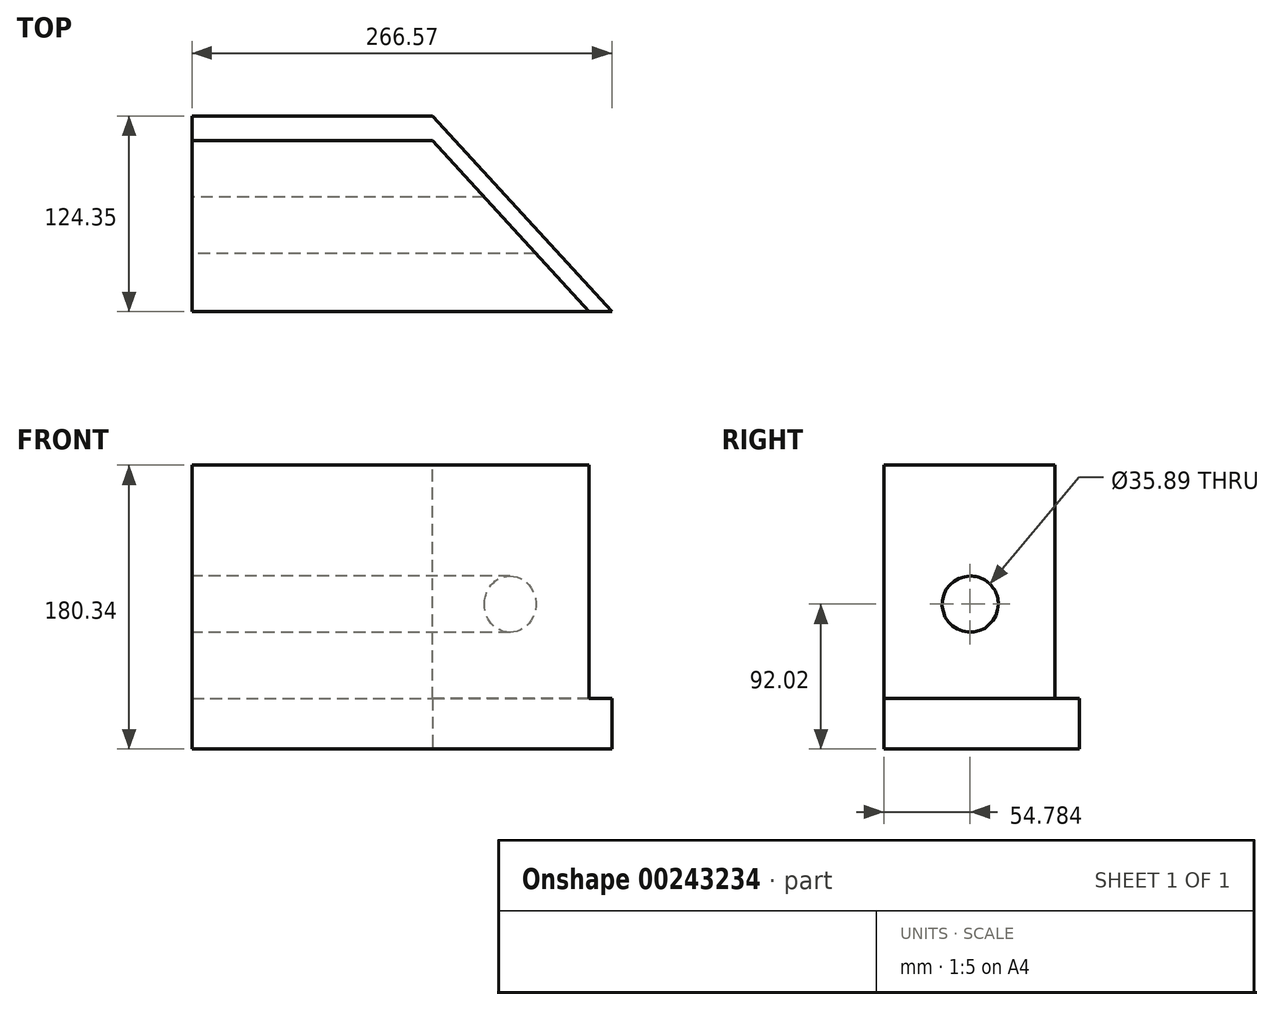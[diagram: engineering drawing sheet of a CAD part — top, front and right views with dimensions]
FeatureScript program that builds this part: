
annotation { "Feature Type Name" : "Feature", "Feature Type Description" : "" }
export const myFeature = defineFeature(function(context is Context, id is Id, definition is map)
    precondition{}
    {
        {
            var Q0;
            Q0=qCreatedBy(makeId("Top.planeOp"),FACE);
            var sketch = newSketch(context, id + "F0", { "sketchPlane" : qUnion([Q0])});
            skLineSegment(sketch, "E0.bottom", {"start": v(-76.3, 35.97) * mm, "end": v(76.5, 35.97) * mm});
            skLineSegment(sketch, "E0.top", {"start": v(-76.3, -72.6) * mm, "end": v(76.5, -72.6) * mm});
            skLineSegment(sketch, "E0.left", {"start": v(-76.3, 35.97) * mm, "end": v(-76.3, -72.6) * mm});
            skLineSegment(sketch, "E1", {"start": v(76.5, -72.6) * mm, "end": v(175.83, -72.6) * mm});
            skLineSegment(sketch, "E2", {"start": v(175.83, -72.6) * mm, "end": v(76.5, 35.97) * mm});
            skSolve(sketch);
        }
        {
            var Q0;
            Q0=makeQuery(id+"F0.imprint","IMPRINT",FACE,{"disambiguationData":[TD([[makeQuery(id+"F0.imprint","IMPRINT",EDGE,{"derivedFrom":sQuery(id+"F0.wireOp",EDGE,"E0.bottom")}),-1.0]])]});
            extrude(context, id + "F1", {"entities" : qUnion([Q0]), "oppositeDirection" : true, "depth" : 180.34 * mm});
        }
        {
            var Q0;
            Q0=makeQuery(id+"F1.opExtrude","CAP_FACE",FACE,{"disambiguationData":[OSD([sQuery(id+"F0.wireOp",EDGE,"E0.bottom"),sQuery(id+"F0.wireOp",EDGE,"E0.top"),sQuery(id+"F0.wireOp",EDGE,"E0.left"),sQuery(id+"F0.wireOp",EDGE,"E1"),sQuery(id+"F0.wireOp",EDGE,"E2")])],"isStart":false});
            var sketch = newSketch(context, id + "F2", { "sketchPlane" : qUnion([Q0])});
            skLineSegment(sketch, "E3.bottom", {"start": v(76.5, -51.74) * mm, "end": v(-76.3, -51.74) * mm});
            skLineSegment(sketch, "E3.top", {"start": v(76.5, 72.6) * mm, "end": v(-76.3, 72.6) * mm});
            skLineSegment(sketch, "E3.right", {"start": v(-76.3, -51.74) * mm, "end": v(-76.3, 72.6) * mm});
            skLineSegment(sketch, "E4", {"start": v(76.5, -51.74) * mm, "end": v(190.26, 72.6) * mm});
            skLineSegment(sketch, "E5", {"start": v(190.26, 72.6) * mm, "end": v(76.5, 72.6) * mm});
            skSolve(sketch);
        }
        {
            var Q0;
            {var subQ5=sQuery(id+"F2.wireOp",EDGE,"E3.bottom");Q0=makeQuery(id+"F2.imprint","IMPRINT",FACE,{"disambiguationData":[TD([[makeQuery(id+"F2.imprint","IMPRINT",EDGE,{"derivedFrom":subQ5}),-1.0]])]});}
            extrude(context, id + "F3", {"entities" : qUnion([Q0]), "operationType" : NewBodyOperationType.ADD, "oppositeDirection" : true, "depth" : 32 * mm});
        }
        {
            var Q0;
            Q0=makeQuery(id+"F3.boolean.opBoolean","MERGE",FACE,{"derivedFrom":[makeQuery(id+"F1.opExtrude","SWEPT_FACE",FACE,{"disambiguationData":[OSD([sQuery(id+"F0.wireOp",EDGE,"E0.left")])]}),makeQuery(id+"F3.opExtrude","SWEPT_FACE",FACE,{"disambiguationData":[OSD([sQuery(id+"F2.wireOp",EDGE,"E3.right")])]})]});
            var sketch = newSketch(context, id + "F4", { "sketchPlane" : qUnion([Q0])});
            skCircle(sketch, "E6", {"center": v(17.83, -88.32) * mm, "radius": 17.95 * mm});
            skSolve(sketch);
        }
        {
            var Q0;
            Q0=makeQuery(id+"F4.imprint","IMPRINT",FACE,{"disambiguationData":[TD([[makeQuery(id+"F4.imprint","IMPRINT",EDGE,{"derivedFrom":sQuery(id+"F4.wireOp",EDGE,"E6")}),1.0]])]});
            extrude(context, id + "F5", {"entities" : qUnion([Q0]), "operationType" : NewBodyOperationType.REMOVE, "oppositeDirection" : true, "depth" : 340.36 * mm});
        }
    });
